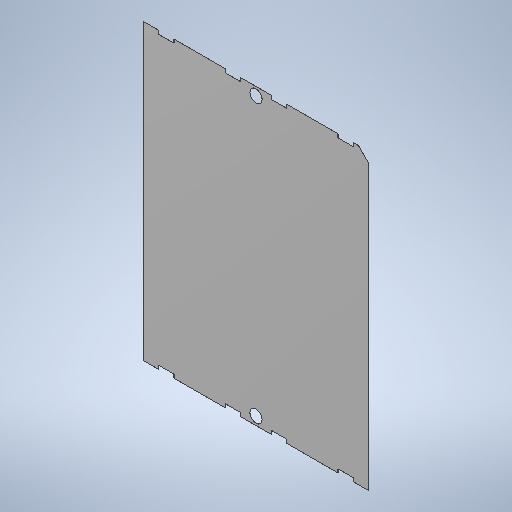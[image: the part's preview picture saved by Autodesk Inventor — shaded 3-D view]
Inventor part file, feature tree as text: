
AUTODESK INVENTOR PART (.ipt)
format: ipt  version: 2025 (Build 290162000, 162)  size: 245,248 bytes
history: native  units: mm
features: extrude x1, sketch x1, imported_body x1
ambient origin geometry x8: Origin, YZ Plane, XZ Plane, XY Plane, X Axis, Y Axis, Z Axis, Center Point
bodies: Solid1 (feature_tree)
feature tree (3):
  extrude  "Extrusion1"  Depth=44.099993mm
  sketch  "Sketch1"  dims[d0=0.0mm d1=0.0mm d2=2.4mm d3=2.4mm d4=1.6mm d5=44.099993mm d6=22.049997mm d7=1.6mm]
  imported_body  "Base1"
